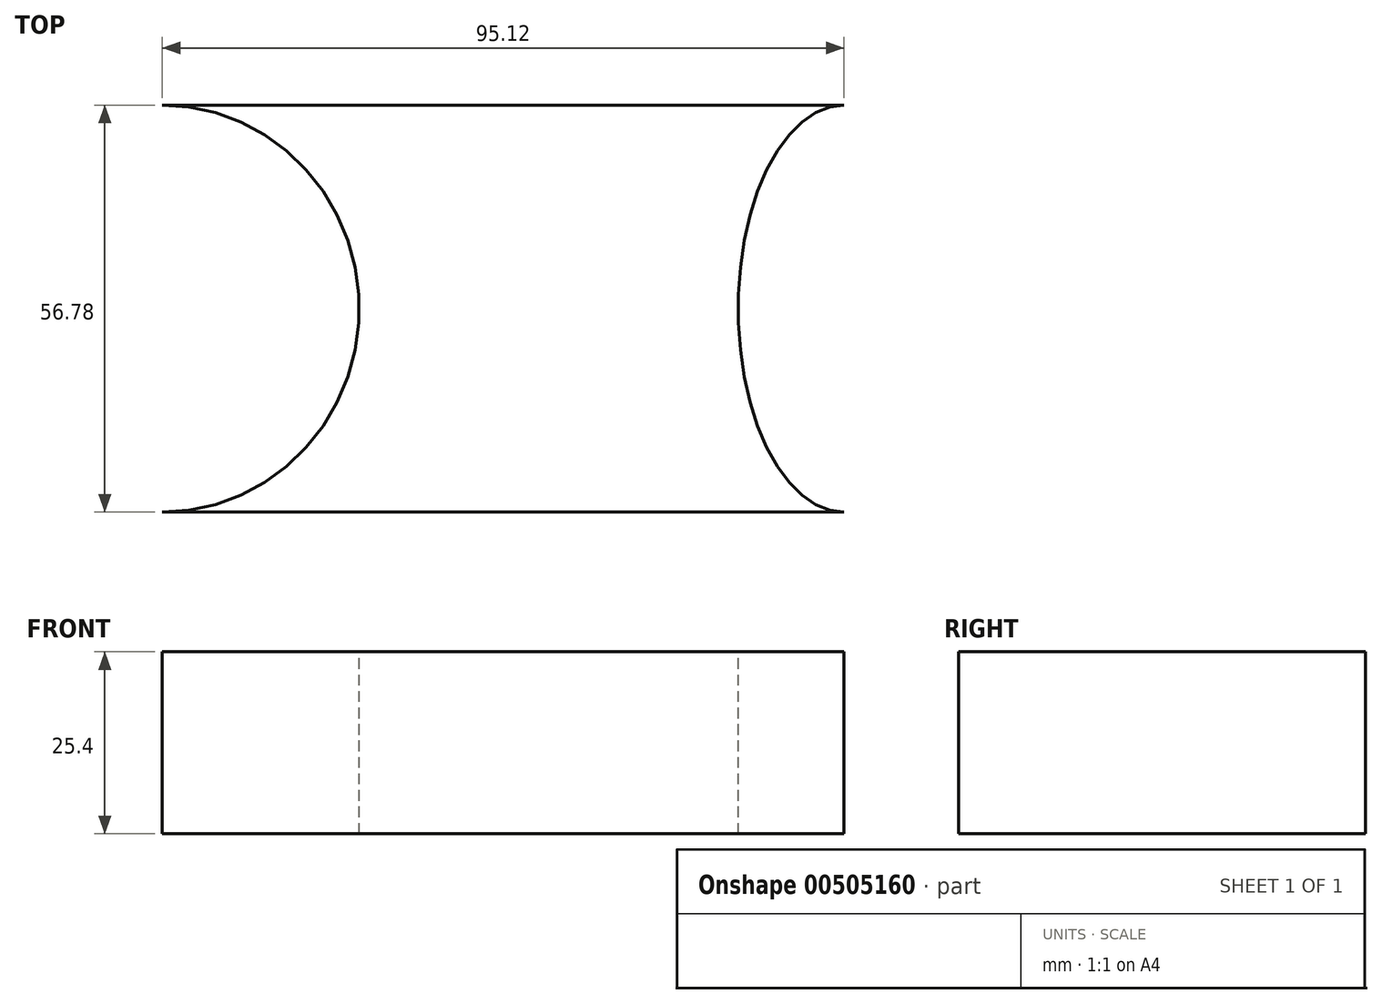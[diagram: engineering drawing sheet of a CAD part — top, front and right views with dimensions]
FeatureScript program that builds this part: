
annotation { "Feature Type Name" : "Feature", "Feature Type Description" : "" }
export const myFeature = defineFeature(function(context is Context, id is Id, definition is map)
    precondition{}
    {
        {
            var Q0;
            Q0=qCreatedBy(makeId("Top.planeOp"),FACE);
            var sketch = newSketch(context, id + "F0", { "sketchPlane" : qUnion([Q0])});
            skLineSegment(sketch, "E0.bottom", {"start": v(-47.56, 28.4) * mm, "end": v(47.56, 28.4) * mm});
            skLineSegment(sketch, "E0.top", {"start": v(-47.56, -28.4) * mm, "end": v(47.56, -28.4) * mm});
            skLineSegment(sketch, "E0.left", {"start": v(-47.56, 28.4) * mm, "end": v(-47.56, -28.4) * mm});
            skLineSegment(sketch, "E0.right", {"start": v(47.56, 28.4) * mm, "end": v(47.56, -28.4) * mm});
            skPoint(sketch, "E0.middle", {"position": v(0, 0) * mm});
            skEllipse(sketch, "E1", {"center": v(-47.56, 0) * mm, "majorRadius": 28.4 * mm, "minorRadius": 27.47 * mm, "majorAxis": v(0, 1)});
            skEllipse(sketch, "E2", {"center": v(47.56, 0) * mm, "majorRadius": 28.4 * mm, "minorRadius": 14.75 * mm, "majorAxis": v(0, 1)});
            skLineSegment(sketch, "E3", {"start": v(47.56, 28.4) * mm, "end": v(-47.56, 28.4) * mm});
            skLineSegment(sketch, "E4", {"start": v(-47.56, 28.4) * mm, "end": v(-47.56, -29.92) * mm});
            skSolve(sketch);
        }
        {
            var Q0;
            {var subQ0=sQuery(id+"F0.wireOp",EDGE,"E0.top");Q0=makeQuery(id+"F0.imprint","IMPRINT",FACE,{"disambiguationData":[TD([[makeQuery(id+"F0.imprint","IMPRINT",EDGE,{"derivedFrom":subQ0}),1.0]])]});}
            extrude(context, id + "F1", {"entities" : qUnion([Q0]), "depth" : 25.4 * mm, "offsetDistance" : 25.4 * mm});
        }
    });
